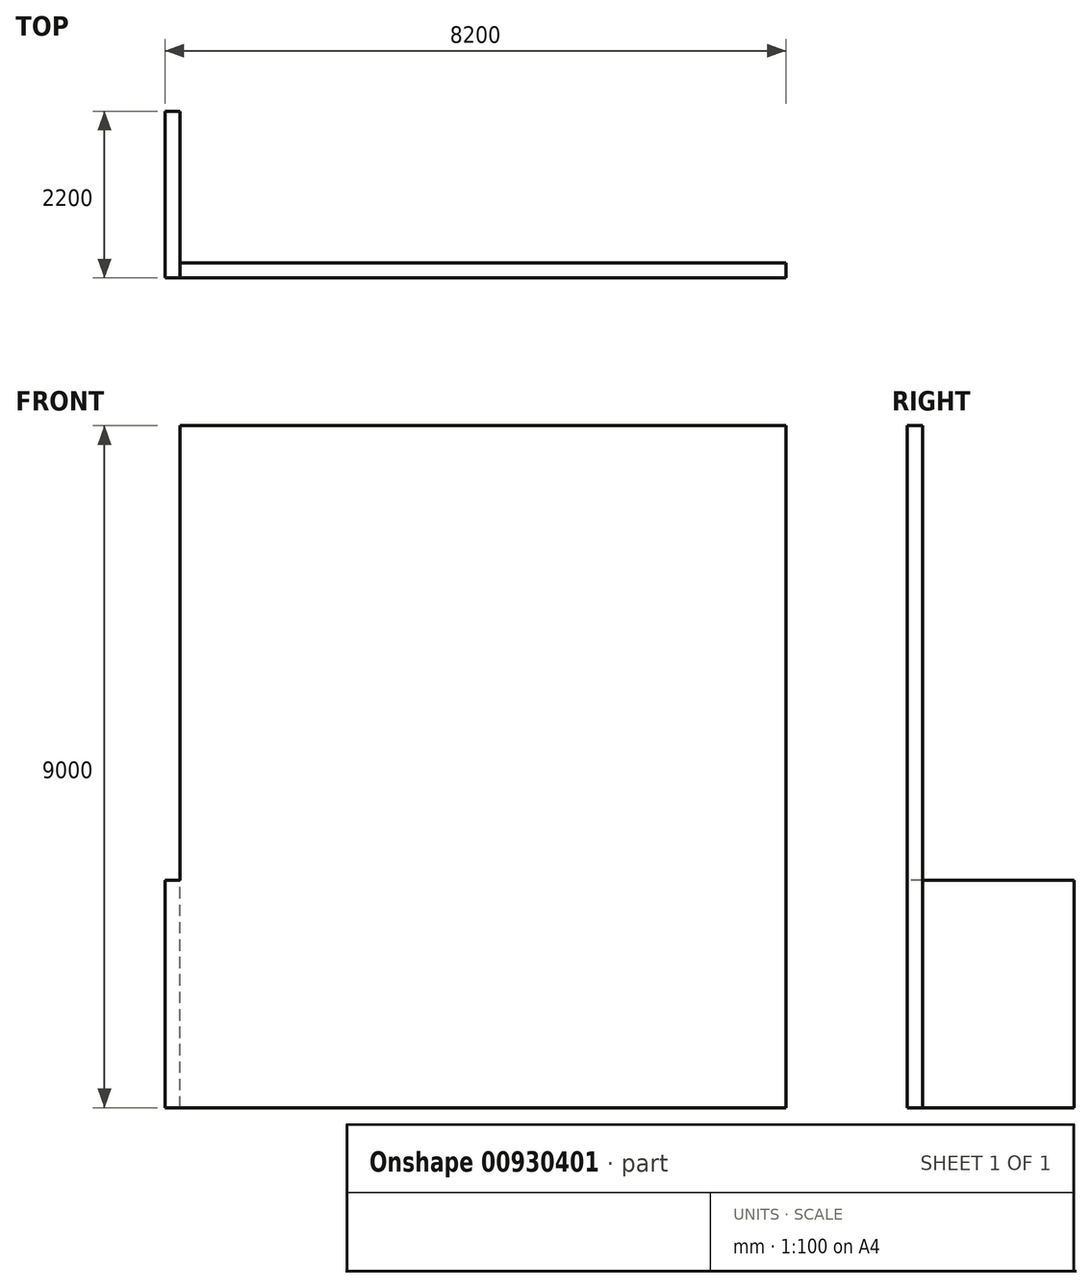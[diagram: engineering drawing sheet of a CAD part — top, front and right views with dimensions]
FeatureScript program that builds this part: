
annotation { "Feature Type Name" : "Feature", "Feature Type Description" : "" }
export const myFeature = defineFeature(function(context is Context, id is Id, definition is map)
    precondition{}
    {
        {
            var Q0;
            Q0=qCreatedBy(makeId("Front.planeOp"),FACE);
            var sketch = newSketch(context, id + "F0", { "sketchPlane" : qUnion([Q0])});
            skLineSegment(sketch, "E0.bottom", {"start": v(0, 0) * mm, "end": v(8000, 0) * mm});
            skLineSegment(sketch, "E0.top", {"start": v(0, 9000) * mm, "end": v(8000, 9000) * mm});
            skLineSegment(sketch, "E0.left", {"start": v(0, 0) * mm, "end": v(0, 9000) * mm});
            skLineSegment(sketch, "E0.right", {"start": v(8000, 0) * mm, "end": v(8000, 9000) * mm});
            skLineSegment(sketch, "E1.bottom", {"start": v(0, 0) * mm, "end": v(-200, 0) * mm});
            skLineSegment(sketch, "E1.top", {"start": v(0, 3000) * mm, "end": v(-200, 3000) * mm});
            skLineSegment(sketch, "E1.left", {"start": v(0, 0) * mm, "end": v(0, 3000) * mm});
            skLineSegment(sketch, "E1.right", {"start": v(-200, 0) * mm, "end": v(-200, 3000) * mm});
            skSolve(sketch);
        }
        {
            var Q0;
            Q0=makeQuery(id+"F0.imprint","IMPRINT",FACE,{"disambiguationData":[TD([[makeQuery(id+"F0.imprint","IMPRINT",EDGE,{"derivedFrom":sQuery(id+"F0.wireOp",EDGE,"E0.bottom")}),1.0]])]});
            extrude(context, id + "F1", {"entities" : qUnion([Q0]), "oppositeDirection" : true, "depth" : 200 * mm, "offsetDistance" : 25 * mm});
        }
        {
            var Q0;
            Q0=makeQuery(id+"F0.imprint","IMPRINT",FACE,{"disambiguationData":[TD([[makeQuery(id+"F0.imprint","IMPRINT",EDGE,{"derivedFrom":sQuery(id+"F0.wireOp",EDGE,"E1.bottom")}),-1.0]])]});
            extrude(context, id + "F2", {"entities" : qUnion([Q0]), "operationType" : NewBodyOperationType.ADD, "oppositeDirection" : true, "depth" : 2200 * mm, "offsetDistance" : 25 * mm});
        }
    });
